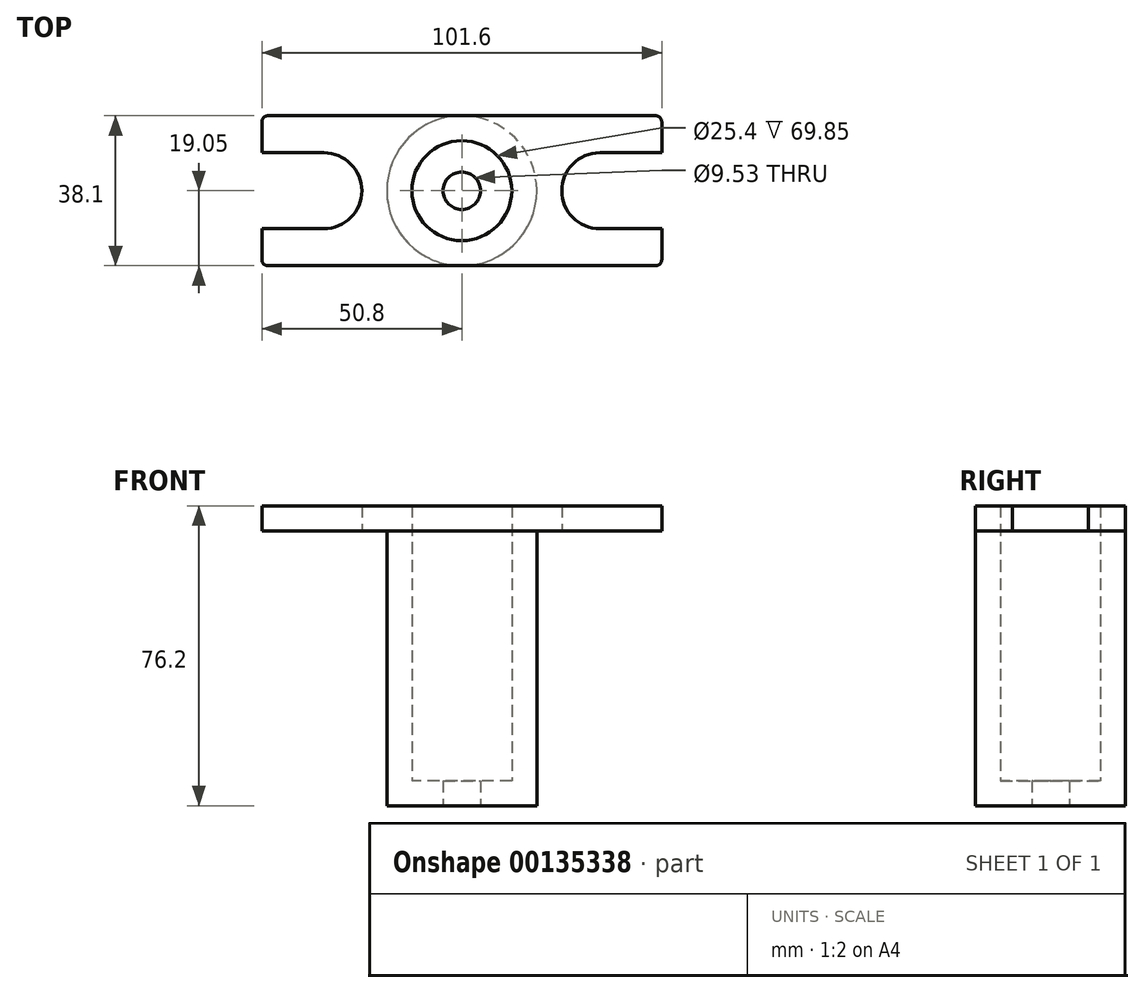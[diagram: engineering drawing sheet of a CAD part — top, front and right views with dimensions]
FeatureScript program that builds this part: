
annotation { "Feature Type Name" : "Feature", "Feature Type Description" : "" }
export const myFeature = defineFeature(function(context is Context, id is Id, definition is map)
    precondition{}
    {
        {
            var Q0;
            Q0=qCreatedBy(makeId("Top.planeOp"),FACE);
            var sketch = newSketch(context, id + "F0", { "sketchPlane" : qUnion([Q0])});
            skLineSegment(sketch, "E0.bottom", {"start": v(50.8, -19.05) * mm, "end": v(-50.8, -19.05) * mm});
            skLineSegment(sketch, "E0.top", {"start": v(50.8, 19.05) * mm, "end": v(-50.8, 19.05) * mm});
            skPoint(sketch, "E0.middle", {"position": v(0, 0) * mm});
            skCircle(sketch, "E1", {"center": v(0, 0) * mm, "radius": 12.7 * mm});
            skCircle(sketch, "E2", {"center": v(0, 0) * mm, "radius": 4.76 * mm});
            skLineSegment(sketch, "E3", {"start": v(0, 0) * mm, "end": v(-35.05, 0) * mm, "construction": true});
            skArc(sketch, "E4", {"start": v(-35.05, 9.65) * mm, "mid": v(-25.4, 0) * mm, "end": v(-35.05, -9.65) * mm});
            skLineSegment(sketch, "E5", {"start": v(0, 34.25) * mm, "end": v(0, 43.77) * mm, "construction": true});
            skPoint(sketch, "E5.startSnap0", {"position": v(0, 19.05) * mm});
            skArc(sketch, "E6.MirrorCS", {"start": v(35.05, 9.65) * mm, "mid": v(25.4, 0) * mm, "end": v(35.05, -9.65) * mm});
            skLineSegment(sketch, "E7", {"start": v(-50.8, 9.65) * mm, "end": v(-35.05, 9.65) * mm});
            skLineSegment(sketch, "E8", {"start": v(-50.8, 19.05) * mm, "end": v(-50.8, 9.65) * mm});
            skLineSegment(sketch, "E9", {"start": v(-35.05, -9.65) * mm, "end": v(-50.8, -9.65) * mm});
            skLineSegment(sketch, "E10", {"start": v(-50.8, -9.65) * mm, "end": v(-50.8, -19.05) * mm});
            skLineSegment(sketch, "E11.MirrorCS", {"start": v(50.8, 19.05) * mm, "end": v(50.8, 9.65) * mm});
            skLineSegment(sketch, "E12.MirrorCS", {"start": v(50.8, 9.65) * mm, "end": v(35.05, 9.65) * mm});
            skLineSegment(sketch, "E13.MirrorCS", {"start": v(35.05, -9.65) * mm, "end": v(50.8, -9.65) * mm});
            skLineSegment(sketch, "E14.MirrorCS", {"start": v(50.8, -9.65) * mm, "end": v(50.8, -19.05) * mm});
            skSolve(sketch);
        }
        {
            var Q0;
            Q0 = qSketchRegion(id + "F0", true);
            extrude(context, id + "F1", {"entities" : qUnion([Q0]), "depth" : 6.35 * mm});
        }
        {
            var Q0;
            Q0=makeQuery(id+"F1.opExtrude","SWEPT_EDGE",EDGE,{"disambiguationData":[OSD([sQuery(id+"F0.wireOp",EDGE,"E0.top"),sQuery(id+"F0.wireOp",EDGE,"E8")])]});
            var Q1;
            Q1=makeQuery(id+"F1.opExtrude","SWEPT_EDGE",EDGE,{"disambiguationData":[OSD([sQuery(id+"F0.wireOp",EDGE,"E0.top"),sQuery(id+"F0.wireOp",EDGE,"E11.MirrorCS")])]});
            var Q2;
            Q2=makeQuery(id+"F1.opExtrude","SWEPT_EDGE",EDGE,{"disambiguationData":[OSD([sQuery(id+"F0.wireOp",EDGE,"E0.bottom"),sQuery(id+"F0.wireOp",EDGE,"E14.MirrorCS")])]});
            var Q3;
            Q3=makeQuery(id+"F1.opExtrude","SWEPT_EDGE",EDGE,{"disambiguationData":[OSD([sQuery(id+"F0.wireOp",EDGE,"E0.bottom"),sQuery(id+"F0.wireOp",EDGE,"E10")])]});
            fillet(context, id + "F2", {"entities" : qUnion([Q0, Q1, Q2, Q3]), "radius" : 1.52 * mm, "allowEdgeOverflow" : false});
        }
        {
            var Q0;
            Q0=qCreatedBy(makeId("Right.planeOp"),FACE);
            var sketch = newSketch(context, id + "F3", { "sketchPlane" : qUnion([Q0])});
            skLineSegment(sketch, "E15.bottom", {"start": v(-12.7, 0) * mm, "end": v(-19.05, 0) * mm});
            skLineSegment(sketch, "E15.top", {"start": v(-12.7, -69.85) * mm, "end": v(-19.05, -69.85) * mm});
            skLineSegment(sketch, "E15.left", {"start": v(-12.7, 0) * mm, "end": v(-12.7, -69.85) * mm});
            skLineSegment(sketch, "E15.right", {"start": v(-19.05, 0) * mm, "end": v(-19.05, -69.85) * mm});
            skLineSegment(sketch, "E16", {"start": v(0, 0) * mm, "end": v(0, -33.93) * mm, "construction": true});
            skSolve(sketch);
        }
        {
            var Q0;
            Q0=makeQuery(id+"F3.imprint","IMPRINT",FACE,{"disambiguationData":[TD([[makeQuery(id+"F3.imprint","IMPRINT",EDGE,{"derivedFrom":sQuery(id+"F3.wireOp",EDGE,"E15.bottom")}),1.0]])]});
            var Q1;
            Q1=sQuery(id+"F3.wireOp",EDGE,"E16");
            revolve(context, id + "F4", {"operationType" : NewBodyOperationType.ADD, "entities" : qUnion([Q0]), "axis" : qUnion([Q1]), "revolveType" : RevolveType.FULL});
        }
        {
            var Q0;
            Q0=makeQuery(id+"F4.opRevolve","SWEPT_FACE",FACE,{"disambiguationData":[OSD([sQuery(id+"F3.wireOp",EDGE,"E15.top")])]});
            var sketch = newSketch(context, id + "F5", { "sketchPlane" : qUnion([Q0])});
            skCircle(sketch, "E17", {"center": v(0, 0) * mm, "radius": 4.76 * mm});
            skSolve(sketch);
        }
        {
            var Q0;
            Q0=makeQuery(id+"F5.imprint","IMPRINT",FACE,{"disambiguationData":[TD([[makeQuery(id+"F5.imprint","IMPRINT",EDGE,{"derivedFrom":sQuery(id+"F5.wireOp",EDGE,"E17")}),-1.0]])]});
            extrude(context, id + "F6", {"entities" : qUnion([Q0]), "operationType" : NewBodyOperationType.ADD, "oppositeDirection" : true, "depth" : 6.35 * mm});
        }
    });
